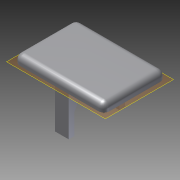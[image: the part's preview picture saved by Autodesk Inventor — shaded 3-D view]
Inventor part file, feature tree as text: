
AUTODESK INVENTOR PART (.ipt)
format: ipt  version: 2012 (Build 160160000, 160)  size: 316,928 bytes
history: native  units: mm
features: extrude x11, sketch x11, projected_geometry x9, reference x4, plane x1, fillet x1
ambient origin geometry x8: Origin, YZ Plane, XZ Plane, XY Plane, X Axis, Y Axis, Z Axis, Center Point
bodies: Solid1 (feature_tree)
feature tree (37):
  extrude  "Extrusion1"  Depth=3.0mm TaperAngle=0.0deg
  plane  "Work Plane1"
  extrude  "Extrusion2"  Depth=0.3mm
  fillet  "Fillet1"  [1 undecoded]
  extrude  "Extrusion3"  Depth=0.3mm
  extrude  "Extrusion4"  Depth=0.3mm
  extrude  "Extrusion5"  TaperAngle=0.0deg  [1 undecoded]
  extrude  "Extrusion6"  Depth=0.3mm
  extrude  "Extrusion7"  Depth=0.3mm
  extrude  "Extrusion8"  Depth=3.0mm TaperAngle=0.0deg
  extrude  "Extrusion9"  Depth=1.5mm
  extrude  "Extrusion10"  Depth=0.891267mm
  extrude  "Extrusion11"  Depth=0.891267mm
  sketch  "Sketch1"  dims[d0=14.9mm d1=0.0mm d2=3.0mm d3=0.0mm]
  reference  "Reference1"
  sketch  "Sketch2"  dims[d4=2.0mm d5=0.3mm d6=0.0mm]
  reference  "Reference2"
  projected_geometry  "Projected Loop1"
  projected_geometry  "Projected Loop2"
  sketch  "Sketch3"  dims[d7=0.3mm d8=0.3mm]
  reference  "Reference3"
  sketch  "Sketch4"  dims[d9=0.3mm d10=0.3mm]
  reference  "Reference4"
  projected_geometry  "Projected Loop3"
  projected_geometry  "Projected Loop4"
  sketch  "Sketch6"  dims[d11=0.3mm d12=0.0mm]
  projected_geometry  "Projected Loop5"
  sketch  "Sketch7"  dims[d13=0.3mm d14=0.3mm]
  projected_geometry  "Projected Loop6"
  projected_geometry  "Projected Loop7"
  sketch  "Sketch8"  dims[d15=1.5mm d16=0.3mm]
  sketch  "Sketch9"  dims[d17=0.3mm d18=3.0mm d19=0.0mm]
  projected_geometry  "Projected Loop8"
  sketch  "Sketch10"  dims[d20=1.5mm d21=1.5mm]
  projected_geometry  "Projected Loop9"
  sketch  "Sketch11"  dims[d22=10.0mm d23=0.0mm d24=0.891267mm]
  sketch  "Sketch12"  dims[d25=0.891267mm d26=0.891267mm d27=10.0mm d28=0.0mm d29=10.0mm d30=0.0mm d31=4.909mm d32=1.909188mm d33=1.499906mm d34=0.0mm d35=2.0mm d36=2.0mm d37=10.0mm d38=0.0mm d39=10.0mm d40=0.0mm d41=10.0mm d42=0.0mm d43=0.4mm d44=0.0mm d45=0.4mm d46=0.0mm]
note: 2 required parameter values undecoded (feature->parameter linkage not recoverable at this tier; creation-order binding heuristic only, values carry confidence <= 0.55)
